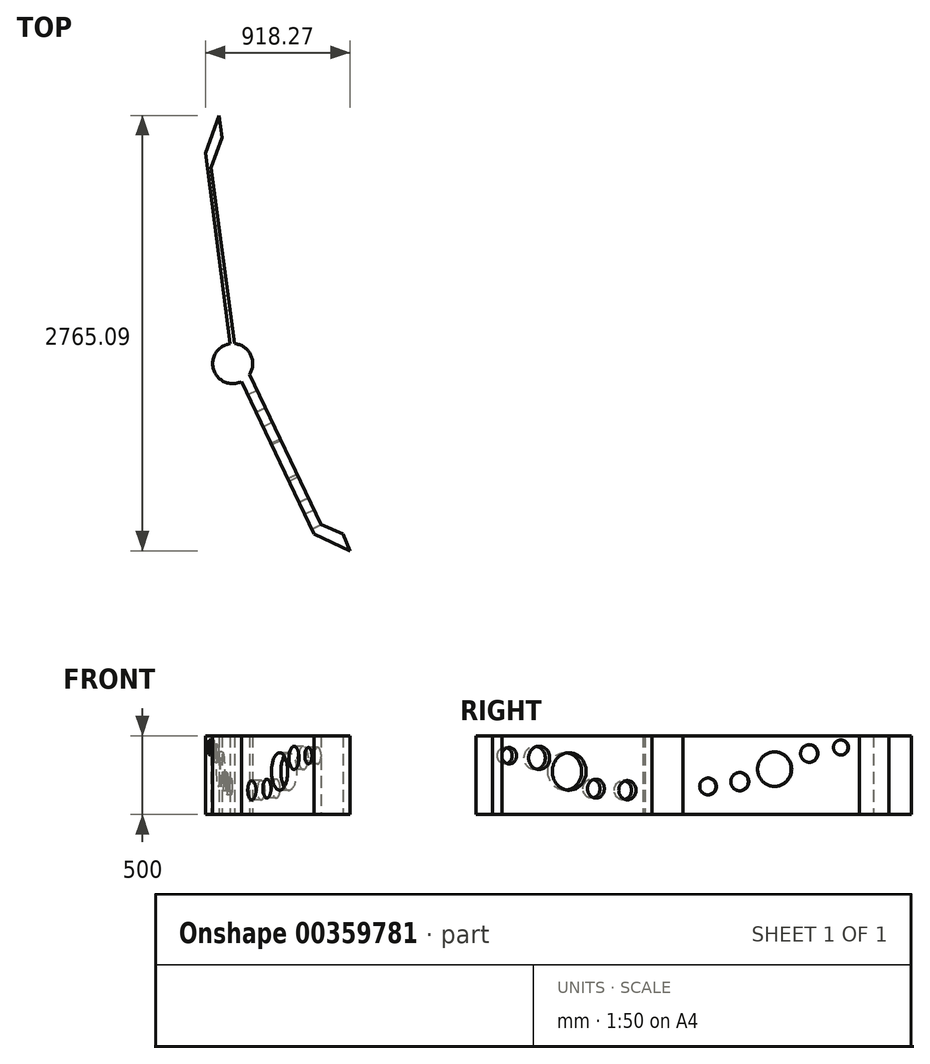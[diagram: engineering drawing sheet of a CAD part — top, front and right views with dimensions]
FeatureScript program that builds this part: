
annotation { "Feature Type Name" : "Feature", "Feature Type Description" : "" }
export const myFeature = defineFeature(function(context is Context, id is Id, definition is map)
    precondition{}
    {
        {
            var Q0;
            Q0=qCreatedBy(makeId("Top.planeOp"),FACE);
            var sketch = newSketch(context, id + "F0", { "sketchPlane" : qUnion([Q0])});
            skCircle(sketch, "E0", {"center": v(0, 0) * mm, "radius": 127 * mm});
            skLineSegment(sketch, "E1", {"start": v(0, 0) * mm, "end": v(-173.4, 1337.42) * mm});
            skLineSegment(sketch, "E2", {"start": v(-173.4, 1337.42) * mm, "end": v(-87.4, 1576.34) * mm});
            skLineSegment(sketch, "E3", {"start": v(-87.4, 1576.34) * mm, "end": v(-68.12, 1435.36) * mm});
            skLineSegment(sketch, "E4", {"start": v(-68.12, 1435.36) * mm, "end": v(-137.3, 1246.16) * mm});
            skLineSegment(sketch, "E5", {"start": v(-137.3, 1246.16) * mm, "end": v(10.67, 126.55) * mm});
            skSolve(sketch);
        }
        {
            var Q0;
            {var subQ0=sQuery(id+"F0.wireOp",EDGE,"E2");Q0=makeQuery(id+"F0.imprint","IMPRINT",FACE,{"disambiguationData":[TD([[makeQuery(id+"F0.imprint","IMPRINT",EDGE,{"derivedFrom":subQ0}),-1.0]])]});}
            var Q1;
            {var subQ0=sQuery(id+"F0.wireOp",EDGE,"E0");var subQ1=makeQuery(id+"F0.imprint","INTERSECT",VERTEX,{"derivedFrom":[subQ0,sQuery(id+"F0.wireOp",EDGE,"E5")]});Q1=makeQuery(id+"F0.imprint","IMPRINT",FACE,{"disambiguationData":[TD([[makeQuery(id+"F0.imprint","IMPRINT",EDGE,{"disambiguationData":[TD([[subQ1,-1.0]])],"derivedFrom":subQ0}),1.0]])]});}
            var Q2;
            Q2 = qSketchRegion(id + "F4", true);
            extrude(context, id + "F1", {"entities" : qUnion([Q0, Q1, Q2]), "depth" : 500 * mm});
        }
        {
            var Q0;
            Q0=makeQuery(id+"F1.opExtrude","SWEPT_FACE",FACE,{"disambiguationData":[OSD([sQuery(id+"F0.wireOp",EDGE,"E1")])]});
            var sketch = newSketch(context, id + "F2", { "sketchPlane" : qUnion([Q0])});
            skCircle(sketch, "E6", {"center": v(-1136.43, 425.62) * mm, "radius": 48.02 * mm});
            skCircle(sketch, "E7", {"center": v(-933, 387.37) * mm, "radius": 56 * mm});
            skCircle(sketch, "E8", {"center": v(-711.09, 287.75) * mm, "radius": 109.5 * mm});
            skCircle(sketch, "E9", {"center": v(-488, 208.43) * mm, "radius": 58.06 * mm});
            skCircle(sketch, "E10", {"center": v(-284.8, 177.88) * mm, "radius": 53.76 * mm});
            skSolve(sketch);
        }
        {
            var Q0;
            Q0=makeQuery(id+"F2.imprint","IMPRINT",FACE,{"disambiguationData":[TD([[makeQuery(id+"F2.imprint","IMPRINT",EDGE,{"derivedFrom":sQuery(id+"F2.wireOp",EDGE,"E6")}),1.0]])]});
            var Q1;
            Q1=makeQuery(id+"F2.imprint","IMPRINT",FACE,{"disambiguationData":[TD([[makeQuery(id+"F2.imprint","IMPRINT",EDGE,{"derivedFrom":sQuery(id+"F2.wireOp",EDGE,"E7")}),1.0]])]});
            var Q2;
            Q2=makeQuery(id+"F2.imprint","IMPRINT",FACE,{"disambiguationData":[TD([[makeQuery(id+"F2.imprint","IMPRINT",EDGE,{"derivedFrom":sQuery(id+"F2.wireOp",EDGE,"E8")}),1.0]])]});
            var Q3;
            Q3=makeQuery(id+"F2.imprint","IMPRINT",FACE,{"disambiguationData":[TD([[makeQuery(id+"F2.imprint","IMPRINT",EDGE,{"derivedFrom":sQuery(id+"F2.wireOp",EDGE,"E9")}),1.0]])]});
            var Q4;
            Q4=makeQuery(id+"F2.imprint","IMPRINT",FACE,{"disambiguationData":[TD([[makeQuery(id+"F2.imprint","IMPRINT",EDGE,{"derivedFrom":sQuery(id+"F2.wireOp",EDGE,"E10")}),1.0]])]});
            extrude(context, id + "F3", {"entities" : qUnion([Q0, Q1, Q2, Q3, Q4]), "operationType" : NewBodyOperationType.REMOVE, "oppositeDirection" : true, "depth" : 50 * mm});
        }
        {
            var Q0;
            Q0=makeQuery(id+"F1.opExtrude","CAP_FACE",FACE,{"disambiguationData":[OSD([sQuery(id+"F0.wireOp",EDGE,"E0"),sQuery(id+"F0.wireOp",EDGE,"E1"),sQuery(id+"F0.wireOp",EDGE,"E2"),sQuery(id+"F0.wireOp",EDGE,"E3"),sQuery(id+"F0.wireOp",EDGE,"E4"),sQuery(id+"F0.wireOp",EDGE,"E5")])],"isStart":true});
            var sketch = newSketch(context, id + "F4", { "sketchPlane" : qUnion([Q0])});
            skLineSegment(sketch, "E11", {"start": v(0, 0) * mm, "end": v(517.14, 1082.85) * mm});
            skLineSegment(sketch, "E12", {"start": v(517.14, 1082.85) * mm, "end": v(744.86, 1188.75) * mm});
            skLineSegment(sketch, "E13", {"start": v(744.86, 1188.75) * mm, "end": v(699.56, 1082.85) * mm});
            skLineSegment(sketch, "E14", {"start": v(699.56, 1082.85) * mm, "end": v(560.77, 1022.55) * mm});
            skCircle(sketch, "E15", {"center": v(0, 0) * mm, "radius": 127.35 * mm});
            skLineSegment(sketch, "E16", {"start": v(560.77, 1022.55) * mm, "end": v(105.9, 70.1) * mm});
            skSolve(sketch);
        }
        {
            var Q0;
            Q0 = qSketchRegion(id + "F4", true);
            extrude(context, id + "F5", {"entities" : qUnion([Q0]), "operationType" : NewBodyOperationType.ADD, "oppositeDirection" : true, "depth" : 500 * mm});
        }
        {
            var Q0;
            Q0=makeQuery(id+"F5.opExtrude","SWEPT_FACE",FACE,{"disambiguationData":[OSD([sQuery(id+"F4.wireOp",EDGE,"E11")])]});
            var sketch = newSketch(context, id + "F6", { "sketchPlane" : qUnion([Q0])});
            skCircle(sketch, "E17", {"center": v(282.94, 154.26) * mm, "radius": 60.74 * mm});
            skCircle(sketch, "E18", {"center": v(504.14, 163.93) * mm, "radius": 59.6 * mm});
            skCircle(sketch, "E19", {"center": v(692.02, 273.25) * mm, "radius": 119.2 * mm});
            skCircle(sketch, "E20", {"center": v(903.65, 359.3) * mm, "radius": 74.24 * mm});
            skCircle(sketch, "E21", {"center": v(1114.4, 373.22) * mm, "radius": 52.07 * mm});
            skSolve(sketch);
        }
        {
            var Q0;
            Q0=makeQuery(id+"F6.imprint","IMPRINT",FACE,{"disambiguationData":[TD([[makeQuery(id+"F6.imprint","IMPRINT",EDGE,{"derivedFrom":sQuery(id+"F6.wireOp",EDGE,"E17")}),1.0]])]});
            var Q1;
            Q1=makeQuery(id+"F6.imprint","IMPRINT",FACE,{"disambiguationData":[TD([[makeQuery(id+"F6.imprint","IMPRINT",EDGE,{"derivedFrom":sQuery(id+"F6.wireOp",EDGE,"E20")}),1.0]])]});
            var Q2;
            Q2=makeQuery(id+"F6.imprint","IMPRINT",FACE,{"disambiguationData":[TD([[makeQuery(id+"F6.imprint","IMPRINT",EDGE,{"derivedFrom":sQuery(id+"F6.wireOp",EDGE,"E21")}),1.0]])]});
            var Q3;
            Q3=makeQuery(id+"F6.imprint","IMPRINT",FACE,{"disambiguationData":[TD([[makeQuery(id+"F6.imprint","IMPRINT",EDGE,{"derivedFrom":sQuery(id+"F6.wireOp",EDGE,"E18")}),1.0]])]});
            var Q4;
            Q4=makeQuery(id+"F6.imprint","IMPRINT",FACE,{"disambiguationData":[TD([[makeQuery(id+"F6.imprint","IMPRINT",EDGE,{"derivedFrom":sQuery(id+"F6.wireOp",EDGE,"E19")}),1.0]])]});
            extrude(context, id + "F7", {"entities" : qUnion([Q0, Q1, Q2, Q3, Q4]), "operationType" : NewBodyOperationType.REMOVE, "oppositeDirection" : true, "depth" : 100 * mm});
        }
    });
